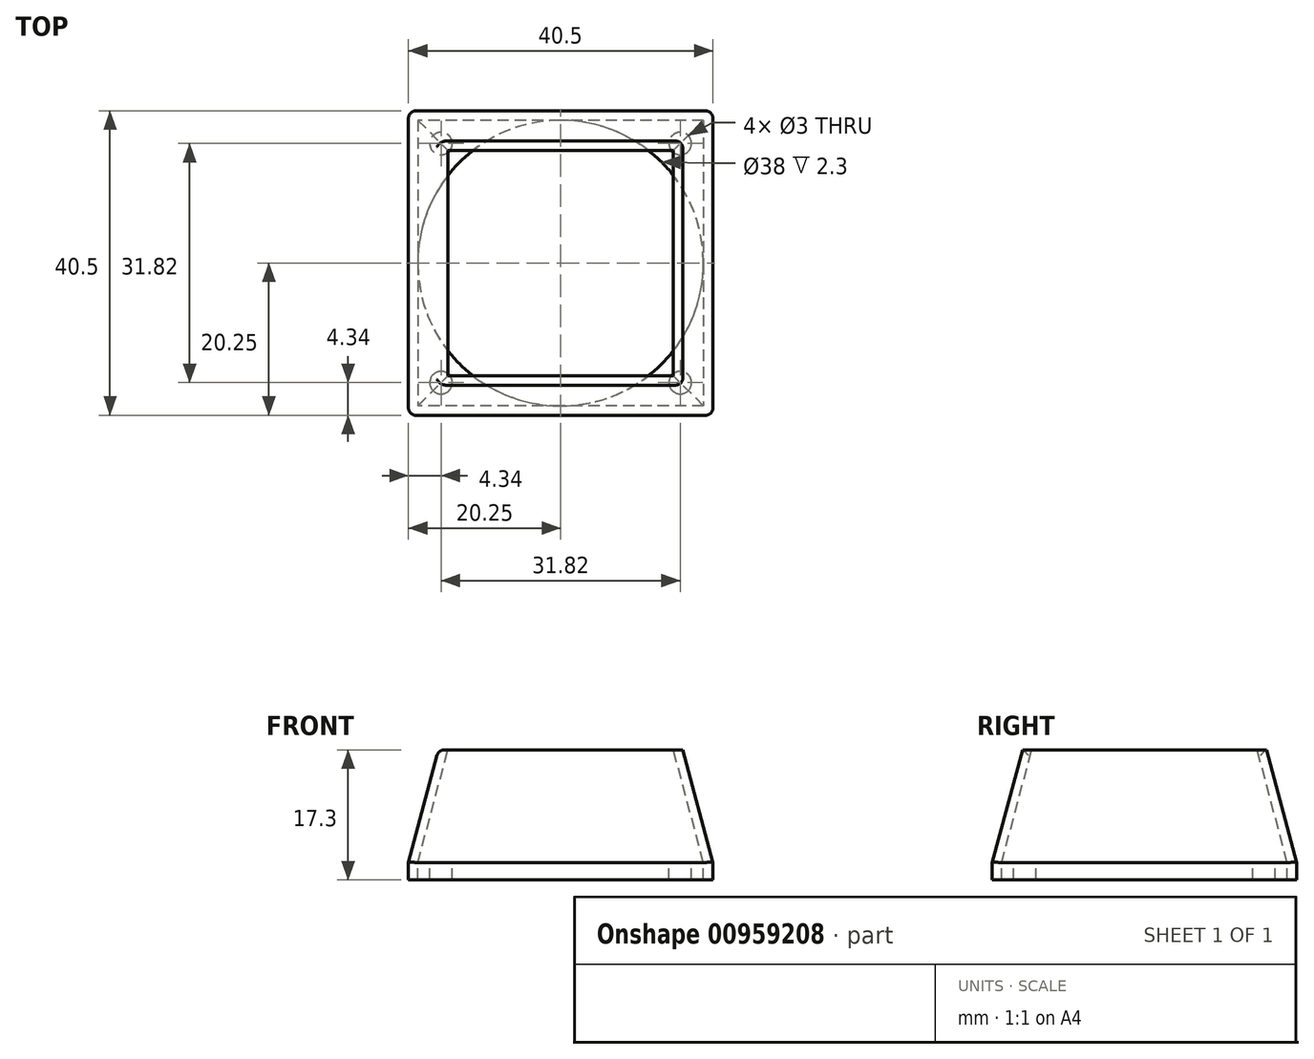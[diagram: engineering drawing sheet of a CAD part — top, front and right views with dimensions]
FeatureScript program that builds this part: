
annotation { "Feature Type Name" : "Feature", "Feature Type Description" : "" }
export const myFeature = defineFeature(function(context is Context, id is Id, definition is map)
    precondition{}
    {
        {
            var Q0;
            Q0=qCreatedBy(makeId("Top.planeOp"),FACE);
            var sketch = newSketch(context, id + "F0", { "sketchPlane" : qUnion([Q0])});
            skLineSegment(sketch, "E0.bottom", {"start": v(20.25, -20.25) * mm, "end": v(-20.25, -20.25) * mm});
            skLineSegment(sketch, "E0.top", {"start": v(20.25, 20.25) * mm, "end": v(-20.25, 20.25) * mm});
            skLineSegment(sketch, "E0.left", {"start": v(20.25, -20.25) * mm, "end": v(20.25, 20.25) * mm});
            skLineSegment(sketch, "E0.right", {"start": v(-20.25, -20.25) * mm, "end": v(-20.25, 20.25) * mm});
            skPoint(sketch, "E0.middle", {"position": v(0, 0) * mm});
            skSolve(sketch);
        }
        {
            var Q0;
            Q0=makeQuery(id+"F0.imprint","IMPRINT",FACE,{"disambiguationData":[TD([[makeQuery(id+"F0.imprint","IMPRINT",EDGE,{"derivedFrom":sQuery(id+"F0.wireOp",EDGE,"E0.bottom")}),-1.0]])]});
            cPlane(context, id + "F1", {"entities" : qUnion([Q0]), "cplaneType" : CPlaneType.OFFSET, "offset" : 15 * mm, "width" : 150 * mm, "height" : 150 * mm});
        }
        {
            var Q0;
            Q0=qCreatedBy(id+"F1.planeOp",FACE);
            var sketch = newSketch(context, id + "F2", { "sketchPlane" : qUnion([Q0])});
            skLineSegment(sketch, "E1.bottom", {"start": v(16.23, -16.23) * mm, "end": v(-16.23, -16.24) * mm});
            skLineSegment(sketch, "E1.top", {"start": v(16.23, 16.24) * mm, "end": v(-16.23, 16.23) * mm});
            skLineSegment(sketch, "E1.left", {"start": v(16.23, -16.23) * mm, "end": v(16.23, 16.23) * mm});
            skLineSegment(sketch, "E1.right", {"start": v(-16.23, -16.23) * mm, "end": v(-16.23, 16.23) * mm});
            skPoint(sketch, "E1.middle", {"position": v(0, 0) * mm});
            skSolve(sketch);
        }
        {
            var Q0;
            Q0=makeQuery(id+"F0.imprint","IMPRINT",FACE,{"disambiguationData":[TD([[makeQuery(id+"F0.imprint","IMPRINT",EDGE,{"derivedFrom":sQuery(id+"F0.wireOp",EDGE,"E0.bottom")}),-1.0]])]});
            var Q1;
            Q1=makeQuery(id+"F2.imprint","IMPRINT",FACE,{"disambiguationData":[TD([[makeQuery(id+"F2.imprint","IMPRINT",EDGE,{"derivedFrom":sQuery(id+"F2.wireOp",EDGE,"E1.bottom")}),-1.0]])]});
            loft(context, id + "F3", {"sheetProfilesArray" : [{ "sheetProfileEntities" : qUnion([Q0]) }, { "sheetProfileEntities" : qUnion([Q1]) }]});
        }
        {
            var Q0;
            Q0=makeQuery(id+"F0.imprint","IMPRINT",FACE,{"disambiguationData":[TD([[makeQuery(id+"F0.imprint","IMPRINT",EDGE,{"derivedFrom":sQuery(id+"F0.wireOp",EDGE,"E0.bottom")}),-1.0]])]});
            var sketch = newSketch(context, id + "F4", { "sketchPlane" : qUnion([Q0])});
            skLineSegment(sketch, "E2.bottom", {"start": v(19, 19) * mm, "end": v(-19, 19) * mm});
            skLineSegment(sketch, "E2.top", {"start": v(19, -19) * mm, "end": v(-19, -19) * mm});
            skLineSegment(sketch, "E2.left", {"start": v(19, 19) * mm, "end": v(19, -19) * mm});
            skLineSegment(sketch, "E2.right", {"start": v(-19, 19) * mm, "end": v(-19, -19) * mm});
            skPoint(sketch, "E2.middle", {"position": v(0, 0) * mm});
            skSolve(sketch);
        }
        {
            var Q0;
            Q0=makeQuery(id+"F3.opLoft","CAP_FACE",FACE,{"disambiguationData":[OSD([makeQuery(id+"F2.imprint","IMPRINT",FACE,{"disambiguationData":[TD([[makeQuery(id+"F2.imprint","IMPRINT",EDGE,{"derivedFrom":sQuery(id+"F2.wireOp",EDGE,"E1.bottom")}),-1.0]])]})])],"isStart":true});
            var sketch = newSketch(context, id + "F5", { "sketchPlane" : qUnion([Q0])});
            skLineSegment(sketch, "E3.bottom", {"start": v(-15, -15) * mm, "end": v(15, -15) * mm});
            skLineSegment(sketch, "E3.top", {"start": v(-15, 15) * mm, "end": v(15, 15) * mm});
            skLineSegment(sketch, "E3.left", {"start": v(-15, -15) * mm, "end": v(-15, 15) * mm});
            skLineSegment(sketch, "E3.right", {"start": v(15, -15) * mm, "end": v(15, 15) * mm});
            skPoint(sketch, "E3.middle", {"position": v(0, 0) * mm});
            skSolve(sketch);
        }
        {
            var Q1;
            Q1=makeQuery(id+"F4.imprint","IMPRINT",FACE,{"disambiguationData":[TD([[makeQuery(id+"F4.imprint","IMPRINT",EDGE,{"derivedFrom":sQuery(id+"F4.wireOp",EDGE,"E2.bottom")}),1.0]])]});
            var Q2;
            Q2=makeQuery(id+"F5.imprint","IMPRINT",FACE,{"disambiguationData":[TD([[makeQuery(id+"F5.imprint","IMPRINT",EDGE,{"derivedFrom":sQuery(id+"F5.wireOp",EDGE,"E3.bottom")}),1.0]])]});
            loft(context, id + "F6", {"operationType" : NewBodyOperationType.REMOVE, "sheetProfilesArray" : [{ "sheetProfileEntities" : qUnion([Q1]) }, { "sheetProfileEntities" : qUnion([Q2]) }]});
        }
        {
            var Q0;
            Q0=makeQuery(id+"F0.imprint","IMPRINT",FACE,{"disambiguationData":[TD([[makeQuery(id+"F0.imprint","IMPRINT",EDGE,{"derivedFrom":sQuery(id+"F0.wireOp",EDGE,"E0.bottom")}),-1.0]])]});
            var sketch = newSketch(context, id + "F7", { "sketchPlane" : qUnion([Q0])});
            skLineSegment(sketch, "E4.bottom", {"start": v(20.25, 20.25) * mm, "end": v(-20.25, 20.25) * mm});
            skLineSegment(sketch, "E4.top", {"start": v(20.25, -20.25) * mm, "end": v(-20.25, -20.25) * mm});
            skLineSegment(sketch, "E4.left", {"start": v(20.25, 20.25) * mm, "end": v(20.25, -20.25) * mm});
            skLineSegment(sketch, "E4.right", {"start": v(-20.25, 20.25) * mm, "end": v(-20.25, -20.25) * mm});
            skPoint(sketch, "E4.middle", {"position": v(0, 0) * mm});
            skCircle(sketch, "E5", {"center": v(0, 0) * mm, "radius": 19 * mm});
            skLineSegment(sketch, "E6", {"start": v(-20.25, -20.25) * mm, "end": v(20.25, 20.25) * mm, "construction": true});
            skLineSegment(sketch, "E7", {"start": v(20.25, -20.25) * mm, "end": v(-20.25, 20.25) * mm, "construction": true});
            skCircle(sketch, "E8", {"center": v(0, 0) * mm, "radius": 22.5 * mm, "construction": true});
            skCircle(sketch, "E9", {"center": v(-15.9, -15.9) * mm, "radius": 1.5 * mm});
            skCircle(sketch, "E10.MirrorC", {"center": v(15.9, -15.9) * mm, "radius": 1.5 * mm});
            skCircle(sketch, "E11.MirrorC", {"center": v(-15.9, 15.9) * mm, "radius": 1.5 * mm});
            skCircle(sketch, "E12.MirrorC", {"center": v(15.9, 15.9) * mm, "radius": 1.5 * mm});
            skSolve(sketch);
        }
        {
            var Q0;
            Q0=makeQuery(id+"F7.imprint","IMPRINT",FACE,{"disambiguationData":[TD([[makeQuery(id+"F7.imprint","IMPRINT",EDGE,{"derivedFrom":sQuery(id+"F7.wireOp",EDGE,"E5")}),-1.0]])]});
            var Q1;
            Q1=makeQuery(id+"F7.imprint","IMPRINT",FACE,{"disambiguationData":[TD([[makeQuery(id+"F7.imprint","IMPRINT",EDGE,{"derivedFrom":sQuery(id+"F7.wireOp",EDGE,"E4.bottom")}),1.0]])]});
            extrude(context, id + "F8", {"entities" : qUnion([Q0, Q1]), "operationType" : NewBodyOperationType.ADD, "oppositeDirection" : true, "depth" : 2.3 * mm, "offsetDistance" : 25 * mm});
        }
        {
            var Q0;
            Q0=makeQuery(id+"F3.opLoft","SWEPT_EDGE",EDGE,{"disambiguationData":[OSD([sQuery(id+"F0.wireOp",EDGE,"E0.bottom"),sQuery(id+"F0.wireOp",EDGE,"E0.right"),sQuery(id+"F2.wireOp",EDGE,"E1.bottom"),sQuery(id+"F2.wireOp",EDGE,"E1.right")])]});
            var Q1;
            Q1=makeQuery(id+"F8.opExtrude","SWEPT_EDGE",EDGE,{"disambiguationData":[OSD([sQuery(id+"F7.wireOp",EDGE,"E4.top"),sQuery(id+"F7.wireOp",EDGE,"E4.right")])]});
            var Q2;
            Q2=makeQuery(id+"F8.opExtrude","SWEPT_EDGE",EDGE,{"disambiguationData":[OSD([sQuery(id+"F7.wireOp",EDGE,"E4.bottom"),sQuery(id+"F7.wireOp",EDGE,"E4.right")])]});
            var Q3;
            Q3=makeQuery(id+"F3.opLoft","SWEPT_EDGE",EDGE,{"disambiguationData":[OSD([sQuery(id+"F0.wireOp",EDGE,"E0.top"),sQuery(id+"F0.wireOp",EDGE,"E0.right"),sQuery(id+"F2.wireOp",EDGE,"E1.top"),sQuery(id+"F2.wireOp",EDGE,"E1.right")])]});
            var Q4;
            Q4=makeQuery(id+"F3.opLoft","SWEPT_EDGE",EDGE,{"disambiguationData":[OSD([sQuery(id+"F0.wireOp",EDGE,"E0.top"),sQuery(id+"F0.wireOp",EDGE,"E0.left"),sQuery(id+"F2.wireOp",EDGE,"E1.top"),sQuery(id+"F2.wireOp",EDGE,"E1.left")])]});
            var Q5;
            Q5=makeQuery(id+"F8.opExtrude","SWEPT_EDGE",EDGE,{"disambiguationData":[OSD([sQuery(id+"F7.wireOp",EDGE,"E4.bottom"),sQuery(id+"F7.wireOp",EDGE,"E4.left")])]});
            var Q6;
            Q6=makeQuery(id+"F3.opLoft","SWEPT_EDGE",EDGE,{"disambiguationData":[OSD([sQuery(id+"F0.wireOp",EDGE,"E0.bottom"),sQuery(id+"F0.wireOp",EDGE,"E0.left"),sQuery(id+"F2.wireOp",EDGE,"E1.bottom"),sQuery(id+"F2.wireOp",EDGE,"E1.left")])]});
            var Q7;
            Q7=makeQuery(id+"F8.opExtrude","SWEPT_EDGE",EDGE,{"disambiguationData":[OSD([sQuery(id+"F7.wireOp",EDGE,"E4.top"),sQuery(id+"F7.wireOp",EDGE,"E4.left")])]});
            var Q8;
            Q8=makeQuery(id+"F3.opLoft","MID_CAP_EDGE",EDGE,{"disambiguationData":[OSD([sQuery(id+"F2.wireOp",EDGE,"E1.bottom"),sQuery(id+"F2.wireOp",EDGE,"E1.top"),sQuery(id+"F2.wireOp",EDGE,"E1.right")])],"capPos":1.0});
            fillet(context, id + "F9", {"entities" : qUnion([Q0, Q1, Q2, Q3, Q4, Q5, Q6, Q7, Q8]), "radius" : 1 * mm, "tangentPropagation" : true, "allowEdgeOverflow" : false});
        }
    });
